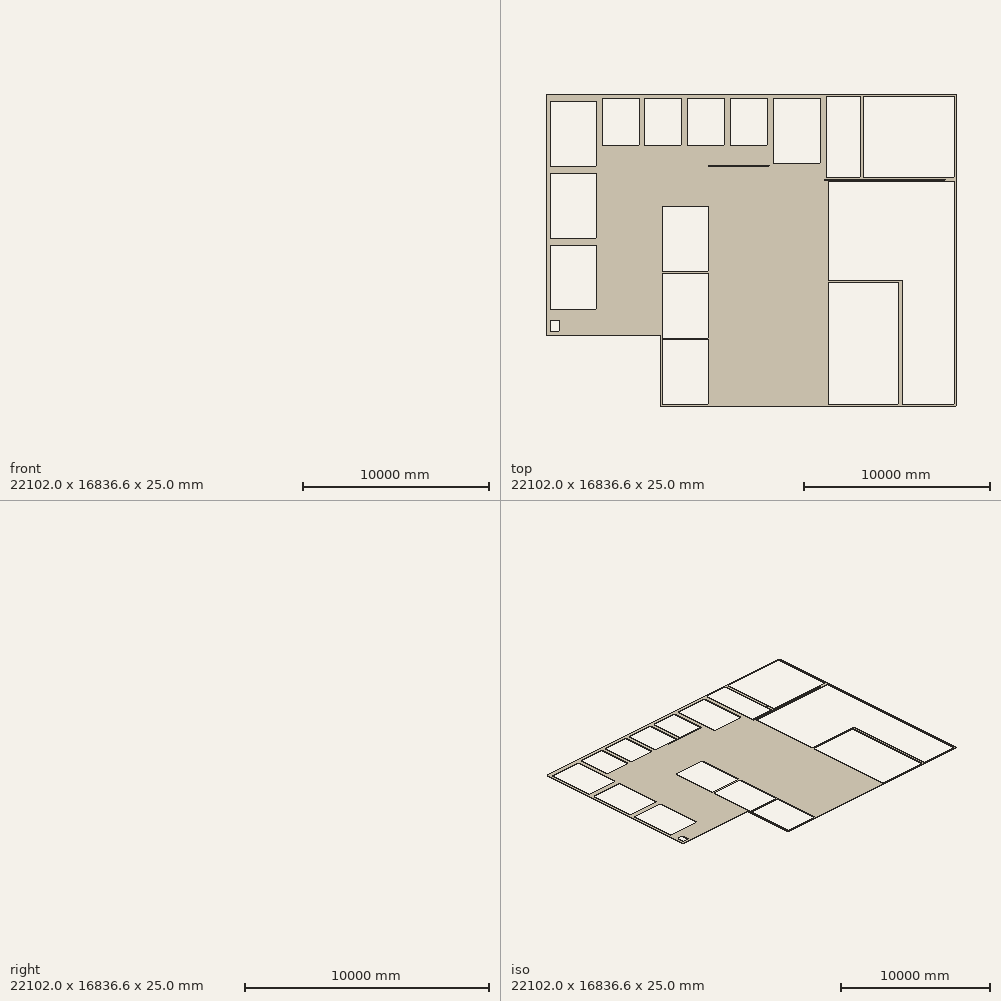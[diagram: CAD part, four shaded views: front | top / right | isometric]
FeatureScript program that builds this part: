
annotation { "Feature Type Name" : "Feature", "Feature Type Description" : "" }
export const myFeature = defineFeature(function(context is Context, id is Id, definition is map)
    precondition{}
    {
        {
            var Q0;
            Q0=qCreatedBy(makeId("Top.planeOp"),FACE);
            var sketch = newSketch(context, id + "F0", { "sketchPlane" : qUnion([Q0])});
            skLineSegment(sketch, "E0.bottom", {"start": v(7500, -6500) * mm, "end": v(-7500, -6500) * mm});
            skLineSegment(sketch, "E0.top", {"start": v(7500, 6500) * mm, "end": v(-7500, 6500) * mm});
            skLineSegment(sketch, "E0.left", {"start": v(7500, -6500) * mm, "end": v(7500, 6500) * mm});
            skLineSegment(sketch, "E0.right", {"start": v(-7500, -6500) * mm, "end": v(-7500, 6500) * mm});
            skLineSegment(sketch, "E1", {"start": v(-4500, -5500) * mm, "end": v(-4500, 3500) * mm});
            skLineSegment(sketch, "E2", {"start": v(-4500, 3500) * mm, "end": v(4500, 3500) * mm});
            skLineSegment(sketch, "E3", {"start": v(4500, 3500) * mm, "end": v(4500, 2500) * mm});
            skLineSegment(sketch, "E4", {"start": v(4500, 2500) * mm, "end": v(7500, 2500) * mm});
            skLineSegment(sketch, "E5", {"start": v(-4500, -5500) * mm, "end": v(-7500, -5500) * mm});
            skLineSegment(sketch, "E6", {"start": v(-7300, -5700) * mm, "end": v(-7300, -6300) * mm});
            skLineSegment(sketch, "E7", {"start": v(-7300, -6300) * mm, "end": v(-6800, -6300) * mm});
            skLineSegment(sketch, "E8", {"start": v(-7300, -5700) * mm, "end": v(-6800, -5700) * mm});
            skLineSegment(sketch, "E9", {"start": v(-6800, -5700) * mm, "end": v(-6800, -6300) * mm});
            skLineSegment(sketch, "E10.bottom", {"start": v(-7300, 6125) * mm, "end": v(-4800, 6125) * mm});
            skLineSegment(sketch, "E10.top", {"start": v(-7300, 2625) * mm, "end": v(-4800, 2625) * mm});
            skLineSegment(sketch, "E10.left", {"start": v(-7300, 6125) * mm, "end": v(-7300, 2625) * mm});
            skLineSegment(sketch, "E10.right", {"start": v(-4800, 6125) * mm, "end": v(-4800, 2625) * mm});
            skLineSegment(sketch, "E11.bottom", {"start": v(-7300, -1625) * mm, "end": v(-4800, -1625) * mm});
            skLineSegment(sketch, "E11.top", {"start": v(-7300, -5125) * mm, "end": v(-4800, -5125) * mm});
            skLineSegment(sketch, "E11.left", {"start": v(-7300, -1625) * mm, "end": v(-7300, -5125) * mm});
            skLineSegment(sketch, "E11.right", {"start": v(-4800, -1625) * mm, "end": v(-4800, -5125) * mm});
            skLineSegment(sketch, "E12.bottom", {"start": v(-7300, 2250) * mm, "end": v(-4800, 2250) * mm});
            skLineSegment(sketch, "E12.top", {"start": v(-7300, -1250) * mm, "end": v(-4800, -1250) * mm});
            skLineSegment(sketch, "E12.left", {"start": v(-7300, 2250) * mm, "end": v(-7300, -1250) * mm});
            skLineSegment(sketch, "E12.right", {"start": v(-4800, 2250) * mm, "end": v(-4800, -1250) * mm});
            skLineSegment(sketch, "E13.bottom", {"start": v(-4500, 6250) * mm, "end": v(-2500, 6250) * mm});
            skLineSegment(sketch, "E13.top", {"start": v(-4500, 3750) * mm, "end": v(-2500, 3750) * mm});
            skLineSegment(sketch, "E13.left", {"start": v(-4500, 6250) * mm, "end": v(-4500, 3750) * mm});
            skLineSegment(sketch, "E13.right", {"start": v(-2500, 6250) * mm, "end": v(-2500, 3750) * mm});
            skLineSegment(sketch, "E14.bottom", {"start": v(-2200, 6250) * mm, "end": v(-200, 6250) * mm});
            skLineSegment(sketch, "E14.top", {"start": v(-2200, 3750) * mm, "end": v(-200, 3750) * mm});
            skLineSegment(sketch, "E14.left", {"start": v(-2200, 6250) * mm, "end": v(-2200, 3750) * mm});
            skLineSegment(sketch, "E14.right", {"start": v(-200, 6250) * mm, "end": v(-200, 3750) * mm});
            skLineSegment(sketch, "E15.bottom", {"start": v(100, 6250) * mm, "end": v(2100, 6250) * mm});
            skLineSegment(sketch, "E15.top", {"start": v(100, 3750) * mm, "end": v(2100, 3750) * mm});
            skLineSegment(sketch, "E15.left", {"start": v(100, 6250) * mm, "end": v(100, 3750) * mm});
            skLineSegment(sketch, "E15.right", {"start": v(2100, 6250) * mm, "end": v(2100, 3750) * mm});
            skLineSegment(sketch, "E16.bottom", {"start": v(2400, 6250) * mm, "end": v(4400, 6250) * mm});
            skLineSegment(sketch, "E16.top", {"start": v(2400, 3750) * mm, "end": v(4400, 3750) * mm});
            skLineSegment(sketch, "E16.left", {"start": v(2400, 6250) * mm, "end": v(2400, 3750) * mm});
            skLineSegment(sketch, "E16.right", {"start": v(4400, 6250) * mm, "end": v(4400, 3750) * mm});
            skLineSegment(sketch, "E17.bottom", {"start": v(1231.44, 3660) * mm, "end": v(4500, 3660) * mm});
            skLineSegment(sketch, "E17.top", {"start": v(1231.44, 3640) * mm, "end": v(4500, 3640) * mm});
            skLineSegment(sketch, "E17.left", {"start": v(1231.44, 3660) * mm, "end": v(1231.44, 3640) * mm});
            skLineSegment(sketch, "E17.right", {"start": v(4500, 3660) * mm, "end": v(4500, 3640) * mm});
            skLineSegment(sketch, "E18.bottom", {"start": v(1227.16, 2640) * mm, "end": v(4502.36, 2640) * mm});
            skLineSegment(sketch, "E18.top", {"start": v(1227.16, 2620) * mm, "end": v(4502.36, 2620) * mm});
            skLineSegment(sketch, "E18.left", {"start": v(1227.16, 2640) * mm, "end": v(1227.16, 2620) * mm});
            skLineSegment(sketch, "E18.right", {"start": v(4502.36, 2640) * mm, "end": v(4502.36, 2620) * mm});
            skLineSegment(sketch, "E19.bottom", {"start": v(4750, 6250) * mm, "end": v(7250, 6250) * mm});
            skLineSegment(sketch, "E19.top", {"start": v(4750, 2750) * mm, "end": v(7250, 2750) * mm});
            skLineSegment(sketch, "E19.left", {"start": v(4750, 6250) * mm, "end": v(4750, 2750) * mm});
            skLineSegment(sketch, "E19.right", {"start": v(7250, 6250) * mm, "end": v(7250, 2750) * mm});
            skLineSegment(sketch, "E20", {"start": v(7500, 6500) * mm, "end": v(14602, 6500) * mm});
            skLineSegment(sketch, "E21", {"start": v(14602, -6500) * mm, "end": v(14602, 6500) * mm});
            skLineSegment(sketch, "E22.bottom", {"start": v(7500, 1900) * mm, "end": v(9500, 1900) * mm});
            skLineSegment(sketch, "E22.top", {"start": v(7500, 1880) * mm, "end": v(9500, 1880) * mm});
            skLineSegment(sketch, "E22.left", {"start": v(7500, 1900) * mm, "end": v(7500, 1880) * mm});
            skLineSegment(sketch, "E22.right", {"start": v(9500, 1900) * mm, "end": v(9500, 1880) * mm});
            skLineSegment(sketch, "E23", {"start": v(9500, 1900) * mm, "end": v(9500, 6500) * mm});
            skLineSegment(sketch, "E24.bottom", {"start": v(7600, 6400) * mm, "end": v(9400, 6400) * mm});
            skLineSegment(sketch, "E24.top", {"start": v(7600, 2000) * mm, "end": v(9400, 2000) * mm});
            skLineSegment(sketch, "E24.left", {"start": v(7600, 6400) * mm, "end": v(7600, 2000) * mm});
            skLineSegment(sketch, "E24.right", {"start": v(9400, 6400) * mm, "end": v(9400, 2000) * mm});
            skLineSegment(sketch, "E25", {"start": v(9500, 1900) * mm, "end": v(14002, 1900) * mm});
            skLineSegment(sketch, "E26", {"start": v(9500, 1880) * mm, "end": v(14002, 1880) * mm});
            skLineSegment(sketch, "E27", {"start": v(14002, 1880) * mm, "end": v(14002, 1900) * mm});
            skLineSegment(sketch, "E28.bottom", {"start": v(9600, 6400) * mm, "end": v(14502, 6400) * mm});
            skLineSegment(sketch, "E28.top", {"start": v(9600, 2000) * mm, "end": v(14502, 2000) * mm});
            skLineSegment(sketch, "E28.left", {"start": v(9600, 6400) * mm, "end": v(9600, 2000) * mm});
            skLineSegment(sketch, "E28.right", {"start": v(14502, 6400) * mm, "end": v(14502, 2000) * mm});
            skLineSegment(sketch, "E29.bottom", {"start": v(9401.96, 2520) * mm, "end": v(9601.96, 2520) * mm});
            skLineSegment(sketch, "E29.top", {"start": v(9401.96, 2500) * mm, "end": v(9601.96, 2500) * mm});
            skLineSegment(sketch, "E29.left", {"start": v(9401.96, 2520) * mm, "end": v(9401.96, 2500) * mm});
            skLineSegment(sketch, "E29.right", {"start": v(9601.96, 2520) * mm, "end": v(9601.96, 2500) * mm});
            skLineSegment(sketch, "E30", {"start": v(7500, -6500) * mm, "end": v(14602, -6500) * mm});
            skLineSegment(sketch, "E31", {"start": v(1343.35, -10336.59) * mm, "end": v(14602, -10336.59) * mm});
            skLineSegment(sketch, "E32", {"start": v(14602, -10336.59) * mm, "end": v(14602, -6500) * mm});
            skLineSegment(sketch, "E33.bottom", {"start": v(1343.35, -10336.59) * mm, "end": v(-1356.65, -10336.59) * mm});
            skLineSegment(sketch, "E33.top", {"start": v(1343.35, 563.41) * mm, "end": v(-1356.65, 563.41) * mm});
            skLineSegment(sketch, "E33.left", {"start": v(1343.35, -10336.59) * mm, "end": v(1343.35, 563.41) * mm});
            skLineSegment(sketch, "E33.right", {"start": v(-1356.65, -10336.59) * mm, "end": v(-1356.65, 563.41) * mm});
            skLineSegment(sketch, "E34.bottom", {"start": v(-1256.65, -10236.59) * mm, "end": v(1243.35, -10236.59) * mm});
            skLineSegment(sketch, "E34.top", {"start": v(-1256.65, -6736.59) * mm, "end": v(1243.35, -6736.59) * mm});
            skLineSegment(sketch, "E34.left", {"start": v(-1256.65, -10236.59) * mm, "end": v(-1256.65, -6736.59) * mm});
            skLineSegment(sketch, "E34.right", {"start": v(1243.35, -10236.59) * mm, "end": v(1243.35, -6736.59) * mm});
            skLineSegment(sketch, "E35.bottom", {"start": v(-1256.65, -3136.59) * mm, "end": v(1243.35, -3136.59) * mm});
            skLineSegment(sketch, "E35.top", {"start": v(-1256.65, -6636.59) * mm, "end": v(1243.35, -6636.59) * mm});
            skLineSegment(sketch, "E35.left", {"start": v(-1256.65, -3136.59) * mm, "end": v(-1256.65, -6636.59) * mm});
            skLineSegment(sketch, "E35.right", {"start": v(1243.35, -3136.59) * mm, "end": v(1243.35, -6636.59) * mm});
            skLineSegment(sketch, "E36.bottom", {"start": v(-1256.65, 463.41) * mm, "end": v(1243.35, 463.41) * mm});
            skLineSegment(sketch, "E36.top", {"start": v(-1256.65, -3036.59) * mm, "end": v(1243.35, -3036.59) * mm});
            skLineSegment(sketch, "E36.left", {"start": v(-1256.65, 463.41) * mm, "end": v(-1256.65, -3036.59) * mm});
            skLineSegment(sketch, "E36.right", {"start": v(1243.35, 463.41) * mm, "end": v(1243.35, -3036.59) * mm});
            skLineSegment(sketch, "E37.bottom", {"start": v(7706.72, 1780) * mm, "end": v(14502, 1780) * mm});
            skLineSegment(sketch, "E37.left", {"start": v(7706.72, 1780) * mm, "end": v(7706.72, -3548.85) * mm});
            skLineSegment(sketch, "E37.right", {"start": v(14502, 1780) * mm, "end": v(14502, -3852.96) * mm});
            skLineSegment(sketch, "E38.bottom", {"start": v(7706.72, -3648.85) * mm, "end": v(11465.4, -3648.85) * mm});
            skLineSegment(sketch, "E38.top", {"start": v(7706.72, -10236.59) * mm, "end": v(11465.4, -10236.59) * mm});
            skLineSegment(sketch, "E38.left", {"start": v(7706.72, -3648.85) * mm, "end": v(7706.72, -10236.59) * mm});
            skLineSegment(sketch, "E38.right", {"start": v(11465.4, -3648.85) * mm, "end": v(11465.4, -10236.59) * mm});
            skLineSegment(sketch, "E39", {"start": v(7706.72, -3548.85) * mm, "end": v(11678.45, -3548.85) * mm});
            skLineSegment(sketch, "E40", {"start": v(11678.45, -3548.85) * mm, "end": v(11678.45, -10236.59) * mm});
            skLineSegment(sketch, "E41", {"start": v(11678.45, -10236.59) * mm, "end": v(14502, -10236.59) * mm});
            skLineSegment(sketch, "E42", {"start": v(14502, -10236.59) * mm, "end": v(14502, -3852.96) * mm});
            skSolve(sketch);
        }
        {
            var Q0;
            Q0 = qSketchRegion(id + "F0", true);
            extrude(context, id + "F1", {"entities" : qUnion([Q0]), "depth" : 25 * mm, "offsetDistance" : 25 * mm});
        }
    });
